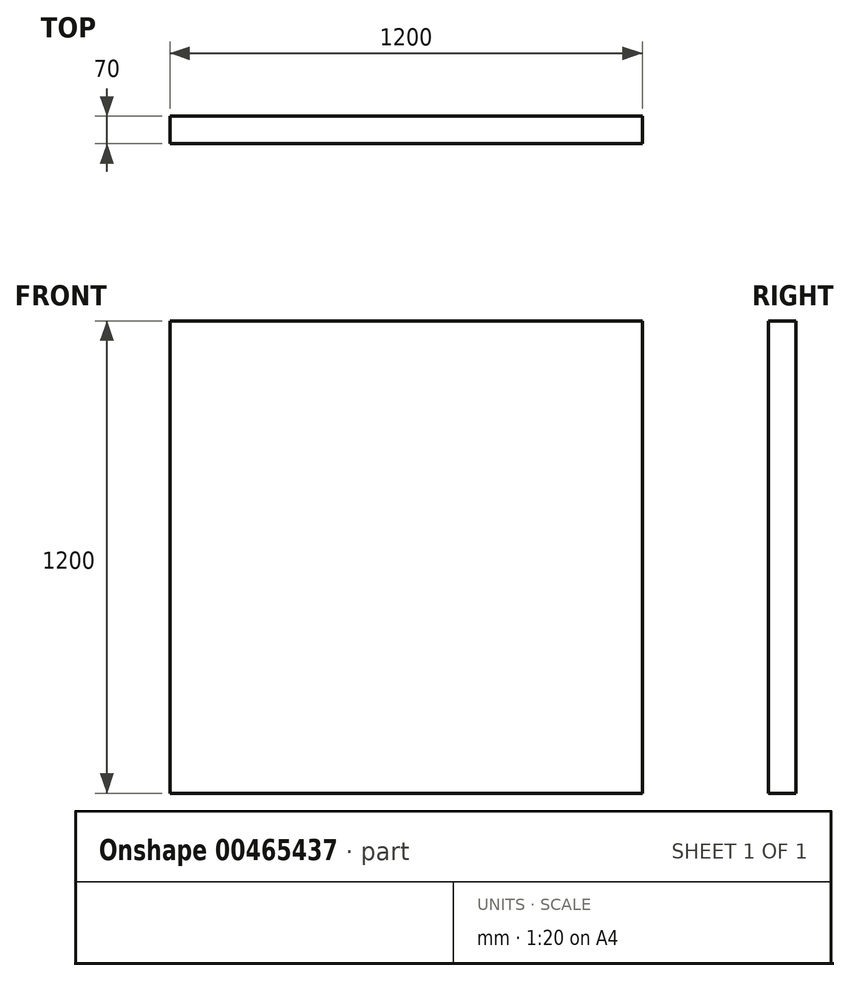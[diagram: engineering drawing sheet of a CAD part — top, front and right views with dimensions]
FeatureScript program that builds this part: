
annotation { "Feature Type Name" : "Feature", "Feature Type Description" : "" }
export const myFeature = defineFeature(function(context is Context, id is Id, definition is map)
    precondition{}
    {
        {
            var Q0;
            Q0=qCreatedBy(makeId("Top.planeOp"),FACE);
            var sketch = newSketch(context, id + "F0", { "sketchPlane" : qUnion([Q0])});
            skLineSegment(sketch, "E0.bottom", {"start": v(0, 0) * mm, "end": v(1200, 0) * mm});
            skLineSegment(sketch, "E0.top", {"start": v(0, 70) * mm, "end": v(1200, 70) * mm});
            skLineSegment(sketch, "E0.left", {"start": v(0, 0) * mm, "end": v(0, 70) * mm});
            skLineSegment(sketch, "E0.right", {"start": v(1200, 0) * mm, "end": v(1200, 70) * mm});
            skSolve(sketch);
        }
        {
            var Q0;
            Q0 = qSketchRegion(id + "F0", true);
            extrude(context, id + "F1", {"entities" : qUnion([Q0]), "depth" : 1200 * mm});
        }
    });
